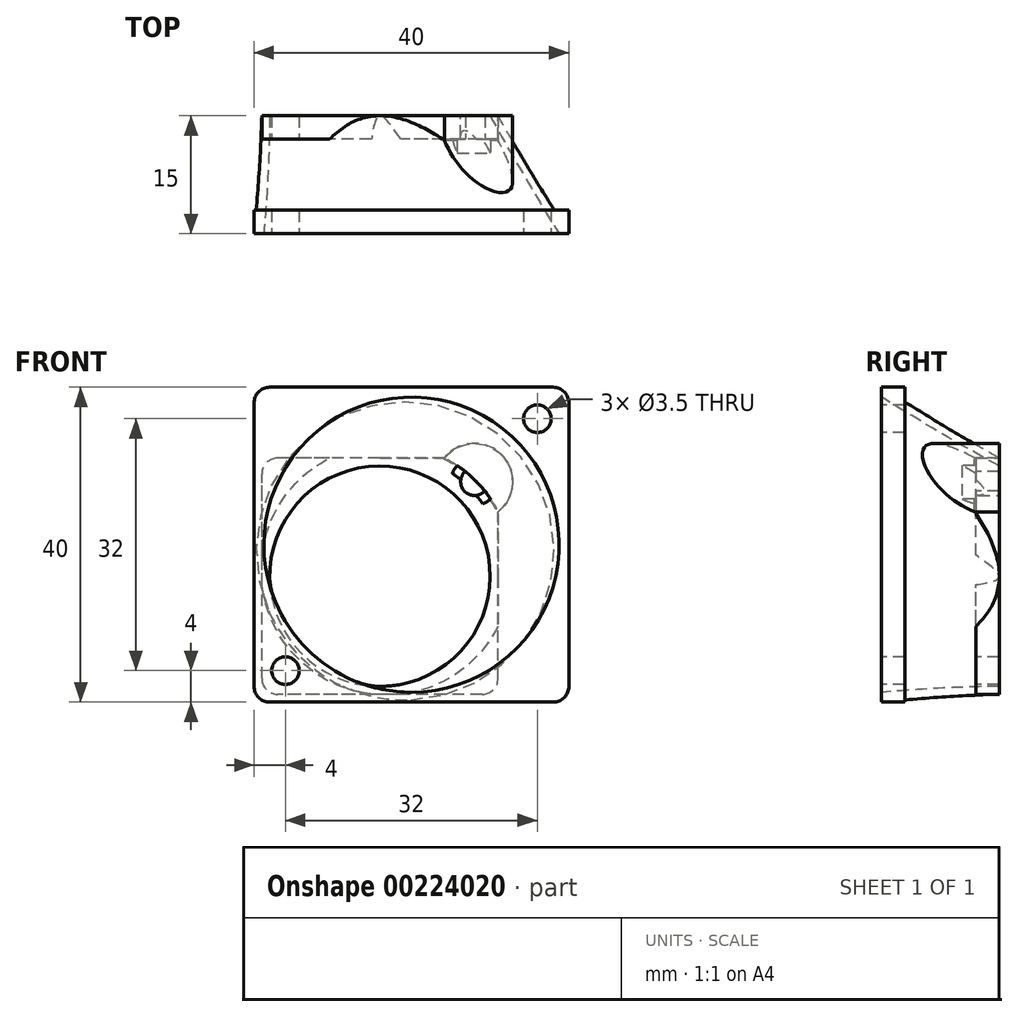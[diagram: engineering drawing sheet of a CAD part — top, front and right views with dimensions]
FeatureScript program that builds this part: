
annotation { "Feature Type Name" : "Feature", "Feature Type Description" : "" }
export const myFeature = defineFeature(function(context is Context, id is Id, definition is map)
    precondition{}
    {
        {
            var Q0;
            Q0=qCreatedBy(makeId("Front.planeOp"),FACE);
            var sketch = newSketch(context, id + "F0", { "sketchPlane" : qUnion([Q0])});
            skLineSegment(sketch, "E0.bottom", {"start": v(0, 0) * mm, "end": v(40, 0) * mm});
            skLineSegment(sketch, "E0.top", {"start": v(0, 40) * mm, "end": v(40, 40) * mm});
            skLineSegment(sketch, "E0.left", {"start": v(0, 0) * mm, "end": v(0, 40) * mm});
            skLineSegment(sketch, "E0.right", {"start": v(40, 0) * mm, "end": v(40, 40) * mm});
            skLineSegment(sketch, "E1", {"start": v(0, 0) * mm, "end": v(40, 40) * mm, "construction": true});
            skLineSegment(sketch, "E2", {"start": v(0, 40) * mm, "end": v(40, 0) * mm, "construction": true});
            skCircle(sketch, "E3", {"center": v(20, 20) * mm, "radius": 20 * mm});
            skSolve(sketch);
        }
        {
            var Q0;
            Q0=makeQuery(id+"F0.imprint","IMPRINT",FACE,{"disambiguationData":[TD([[makeQuery(id+"F0.imprint","IMPRINT",EDGE,{"derivedFrom":sQuery(id+"F0.wireOp",EDGE,"E0.bottom")}),1.0]])]});
            var Q1;
            {var subQ0=sQuery(id+"F0.wireOp",EDGE,"E0.right");var subQ1=sQuery(id+"F0.wireOp",EDGE,"E0.top");var subQ2=makeQuery(id+"F0.imprint","INTERSECT",VERTEX,{"derivedFrom":[subQ1,subQ0]});Q1=makeQuery(id+"F0.imprint","IMPRINT",FACE,{"disambiguationData":[TD([[makeQuery(id+"F0.imprint","IMPRINT",EDGE,{"disambiguationData":[TD([[subQ2,1.0]])],"derivedFrom":subQ1}),-1.0]])]});}
            var Q2;
            {var subQ0=sQuery(id+"F0.wireOp",EDGE,"E0.left");var subQ1=sQuery(id+"F0.wireOp",EDGE,"E0.top");var subQ2=makeQuery(id+"F0.imprint","INTERSECT",VERTEX,{"derivedFrom":[subQ1,subQ0]});Q2=makeQuery(id+"F0.imprint","IMPRINT",FACE,{"disambiguationData":[TD([[makeQuery(id+"F0.imprint","IMPRINT",EDGE,{"disambiguationData":[TD([[subQ2,-1.0]])],"derivedFrom":subQ1}),-1.0]])]});}
            var Q3;
            {var subQ0=sQuery(id+"F0.wireOp",EDGE,"E3");var subQ1=makeQuery(id+"F0.imprint","INTERSECT",VERTEX,{"derivedFrom":[sQuery(id+"F0.wireOp",EDGE,"E0.top"),subQ0]});Q3=makeQuery(id+"F0.imprint","IMPRINT",FACE,{"disambiguationData":[TD([[makeQuery(id+"F0.imprint","IMPRINT",EDGE,{"disambiguationData":[TD([[subQ1,1.0]])],"derivedFrom":subQ0}),1.0]])]});}
            extrude(context, id + "F1", {"entities" : qUnion([Q0, Q1, Q2, Q3]), "oppositeDirection" : true, "depth" : 3 * mm});
        }
        {
            var Q0;
            Q0=qCreatedBy(makeId("Front.planeOp"),FACE);
            cPlane(context, id + "F2", {"entities" : qUnion([Q0]), "cplaneType" : CPlaneType.OFFSET, "offset" : 15 * mm, "oppositeDirection" : true, "width" : 150 * mm, "height" : 150 * mm});
        }
        {
            var Q0;
            Q0=qCreatedBy(id+"F2.planeOp",FACE);
            var sketch = newSketch(context, id + "F3", { "sketchPlane" : qUnion([Q0])});
            skLineSegment(sketch, "E4.bottom", {"start": v(31, 31) * mm, "end": v(1, 31) * mm});
            skLineSegment(sketch, "E4.top", {"start": v(31, 1) * mm, "end": v(1, 1) * mm});
            skLineSegment(sketch, "E4.left", {"start": v(1, 1) * mm, "end": v(1, 31) * mm});
            skLineSegment(sketch, "E4.right", {"start": v(31, 1) * mm, "end": v(31, 31) * mm});
            skLineSegment(sketch, "E5", {"start": v(1, 1) * mm, "end": v(31, 31) * mm, "construction": true});
            skLineSegment(sketch, "E6", {"start": v(1, 31) * mm, "end": v(31, 1) * mm, "construction": true});
            skCircle(sketch, "E7", {"center": v(16, 16) * mm, "radius": 15 * mm});
            skSolve(sketch);
        }
        {
            var Q1;
            {var subQ0=sQuery(id+"F0.wireOp",EDGE,"E3");var subQ1=makeQuery(id+"F0.imprint","INTERSECT",VERTEX,{"derivedFrom":[sQuery(id+"F0.wireOp",EDGE,"E0.top"),subQ0]});Q1=makeQuery(id+"F0.imprint","IMPRINT",FACE,{"disambiguationData":[TD([[makeQuery(id+"F0.imprint","IMPRINT",EDGE,{"disambiguationData":[TD([[subQ1,1.0]])],"derivedFrom":subQ0}),1.0]])]});}
            var Q2;
            {var subQ0=sQuery(id+"F3.wireOp",EDGE,"E7");var subQ1=makeQuery(id+"F3.imprint","INTERSECT",VERTEX,{"derivedFrom":[sQuery(id+"F3.wireOp",EDGE,"E4.top"),subQ0]});Q2=makeQuery(id+"F3.imprint","IMPRINT",FACE,{"disambiguationData":[TD([[makeQuery(id+"F3.imprint","IMPRINT",EDGE,{"disambiguationData":[TD([[subQ1,1.0]])],"derivedFrom":subQ0}),1.0]])]});}
            loft(context, id + "F4", {"operationType" : NewBodyOperationType.ADD, "sheetProfilesArray" : [{ "sheetProfileEntities" : qUnion([Q1]) }, { "sheetProfileEntities" : qUnion([Q2]) }]});
        }
        {
            var Q0;
            Q0 = qSketchRegion(id + "F3", true);
            extrude(context, id + "F5", {"entities" : qUnion([Q0]), "operationType" : NewBodyOperationType.ADD, "depth" : 3 * mm});
        }
        {
            var Q0;
            {var subQ0=sQuery(id+"F0.wireOp",EDGE,"E3");var subQ1=makeQuery(id+"F0.imprint","INTERSECT",VERTEX,{"derivedFrom":[sQuery(id+"F0.wireOp",EDGE,"E0.top"),subQ0]});Q0=makeQuery(id+"F0.imprint","IMPRINT",FACE,{"disambiguationData":[TD([[makeQuery(id+"F0.imprint","IMPRINT",EDGE,{"disambiguationData":[TD([[subQ1,1.0]])],"derivedFrom":subQ0}),1.0]])]});}
            var sketch = newSketch(context, id + "F6", { "sketchPlane" : qUnion([Q0])});
            skPoint(sketch, "E8.0", {"position": v(20, 20) * mm});
            skCircle(sketch, "E9", {"center": v(20, 20) * mm, "radius": 18.75 * mm});
            skSolve(sketch);
        }
        {
            var Q0;
            {var subQ0=sQuery(id+"F3.wireOp",EDGE,"E7");var subQ1=makeQuery(id+"F3.imprint","INTERSECT",VERTEX,{"derivedFrom":[sQuery(id+"F3.wireOp",EDGE,"E4.top"),subQ0]});Q0=makeQuery(id+"F3.imprint","IMPRINT",FACE,{"disambiguationData":[TD([[makeQuery(id+"F3.imprint","IMPRINT",EDGE,{"disambiguationData":[TD([[subQ1,1.0]])],"derivedFrom":subQ0}),1.0]])]});}
            var sketch = newSketch(context, id + "F7", { "sketchPlane" : qUnion([Q0])});
            skPoint(sketch, "E10.0", {"position": v(16, 16) * mm});
            skCircle(sketch, "E11", {"center": v(16, 16) * mm, "radius": 14 * mm});
            skSolve(sketch);
        }
        {
            var Q1;
            Q1 = qSketchRegion(id + "F6", true);
            var Q2;
            Q2 = qSketchRegion(id + "F7", true);
            loft(context, id + "F8", {"operationType" : NewBodyOperationType.REMOVE, "sheetProfilesArray" : [{ "sheetProfileEntities" : qUnion([Q1]) }, { "sheetProfileEntities" : qUnion([Q2]) }]});
        }
        {
            var Q0;
            {var subQ0=sQuery(id+"F0.wireOp",EDGE,"E0.left");var subQ1=sQuery(id+"F0.wireOp",EDGE,"E0.bottom");var subQ2=makeQuery(id+"F0.imprint","INTERSECT",VERTEX,{"derivedFrom":[subQ1,subQ0]});Q0=makeQuery(id+"F0.imprint","IMPRINT",FACE,{"disambiguationData":[TD([[makeQuery(id+"F0.imprint","IMPRINT",EDGE,{"disambiguationData":[TD([[subQ2,-1.0]])],"derivedFrom":subQ1}),1.0]])]});}
            var sketch = newSketch(context, id + "F9", { "sketchPlane" : qUnion([Q0])});
            skCircle(sketch, "E12", {"center": v(4, 4) * mm, "radius": 1.75 * mm});
            skLineSegment(sketch, "E13.0", {"start": v(0, 0) * mm, "end": v(40, 40) * mm, "construction": true});
            skCircle(sketch, "E14", {"center": v(36, 36) * mm, "radius": 1.75 * mm});
            skSolve(sketch);
        }
        {
            var Q0;
            Q0 = qSketchRegion(id + "F9", true);
            extrude(context, id + "F10", {"entities" : qUnion([Q0]), "operationType" : NewBodyOperationType.REMOVE, "endBound" : BoundingType.THROUGH_ALL, "oppositeDirection" : true, "depth" : 25 * mm});
        }
        {
            var Q0;
            {var subQ0=sQuery(id+"F3.wireOp",EDGE,"E4.right");var subQ1=sQuery(id+"F3.wireOp",EDGE,"E4.bottom");var subQ2=makeQuery(id+"F3.imprint","INTERSECT",VERTEX,{"derivedFrom":[subQ1,subQ0]});Q0=makeQuery(id+"F3.imprint","IMPRINT",FACE,{"disambiguationData":[TD([[makeQuery(id+"F3.imprint","IMPRINT",EDGE,{"disambiguationData":[TD([[subQ2,-1.0]])],"derivedFrom":subQ1}),1.0]])]});}
            var sketch = newSketch(context, id + "F11", { "sketchPlane" : qUnion([Q0])});
            skLineSegment(sketch, "E15.0", {"start": v(1, 1) * mm, "end": v(31, 31) * mm, "construction": true});
            skCircle(sketch, "E16", {"center": v(28, 28) * mm, "radius": 1.75 * mm});
            skSolve(sketch);
        }
        {
            var Q0;
            Q0 = qSketchRegion(id + "F11", true);
            extrude(context, id + "F12", {"entities" : qUnion([Q0]), "operationType" : NewBodyOperationType.REMOVE, "endBound" : BoundingType.THROUGH_ALL, "depth" : 25 * mm});
        }
        {
            var Q0;
            {var subQ0=sQuery(id+"F0.wireOp",EDGE,"E0.right");var subQ1=sQuery(id+"F0.wireOp",EDGE,"E0.top");var subQ2=makeQuery(id+"F0.imprint","INTERSECT",VERTEX,{"derivedFrom":[subQ1,subQ0]});Q0=makeQuery(id+"F0.imprint","IMPRINT",FACE,{"disambiguationData":[TD([[makeQuery(id+"F0.imprint","IMPRINT",EDGE,{"disambiguationData":[TD([[subQ2,1.0]])],"derivedFrom":subQ1}),-1.0]])]});}
            var sketch = newSketch(context, id + "F13", { "sketchPlane" : qUnion([Q0])});
            skCircle(sketch, "E17.0", {"center": v(28, 28) * mm, "radius": 1.75 * mm, "construction": true});
            skCircle(sketch, "E18", {"center": v(28, 28) * mm, "radius": 3 * mm});
            skSolve(sketch);
        }
        {
            var Q0;
            Q0=makeQuery(id+"F13.imprint","IMPRINT",FACE,{"disambiguationData":[TD([[makeQuery(id+"F13.imprint","IMPRINT",EDGE,{"derivedFrom":sQuery(id+"F13.wireOp",EDGE,"E18")}),1.0]])]});
            var Q1;
            {var subQ0=sQuery(id+"F3.wireOp",EDGE,"E4.left");var subQ1=sQuery(id+"F3.wireOp",EDGE,"E4.top");var subQ2=sQuery(id+"F3.wireOp",EDGE,"E4.bottom");var subQ3=sQuery(id+"F3.wireOp",EDGE,"E4.right");Q1=makeQuery(id+"F5.boolean.opBoolean","SPLIT",FACE,{"disambiguationData":[TD([makeQuery(id+"F4.opLoft","SWEPT_FACE",FACE,{"disambiguationData":[OSD([sQuery(id+"F0.wireOp",EDGE,"E0.bottom"),sQuery(id+"F0.wireOp",EDGE,"E0.left"),sQuery(id+"F0.wireOp",EDGE,"E3"),subQ1,subQ0,sQuery(id+"F3.wireOp",EDGE,"E7")])]}),makeQuery(id+"F5.opExtrude","SWEPT_FACE",FACE,{"disambiguationData":[OSD([subQ2])]}),makeQuery(id+"F5.opExtrude","SWEPT_FACE",FACE,{"disambiguationData":[OSD([subQ3])]})])],"derivedFrom":makeQuery(id+"F5.opExtrude","CAP_FACE",FACE,{"disambiguationData":[OSD([subQ2,subQ1,subQ0,subQ3])],"isStart":false})});}
            extrude(context, id + "F14", {"entities" : qUnion([Q0]), "operationType" : NewBodyOperationType.REMOVE, "endBound" : BoundingType.UP_TO_SURFACE, "oppositeDirection" : true, "endBoundEntityFace" : qUnion([Q1]), "depth" : 12 * mm});
        }
        {
            var Q0;
            {var subQ0=sQuery(id+"F3.wireOp",EDGE,"E4.left");var subQ1=sQuery(id+"F3.wireOp",EDGE,"E4.top");var subQ2=sQuery(id+"F3.wireOp",EDGE,"E4.bottom");var subQ3=sQuery(id+"F3.wireOp",EDGE,"E4.right");Q0=makeQuery(id+"F14.boolean.opBoolean","MERGE",FACE,{"derivedFrom":[makeQuery(id+"F5.boolean.opBoolean","SPLIT",FACE,{"disambiguationData":[TD([makeQuery(id+"F4.opLoft","SWEPT_FACE",FACE,{"disambiguationData":[OSD([sQuery(id+"F0.wireOp",EDGE,"E0.bottom"),sQuery(id+"F0.wireOp",EDGE,"E0.left"),sQuery(id+"F0.wireOp",EDGE,"E3"),subQ1,subQ0,sQuery(id+"F3.wireOp",EDGE,"E7")])]}),makeQuery(id+"F5.opExtrude","SWEPT_FACE",FACE,{"disambiguationData":[OSD([subQ2])]}),makeQuery(id+"F5.opExtrude","SWEPT_FACE",FACE,{"disambiguationData":[OSD([subQ3])]})])],"derivedFrom":makeQuery(id+"F5.opExtrude","CAP_FACE",FACE,{"disambiguationData":[OSD([subQ2,subQ1,subQ0,subQ3])],"isStart":false})}),makeQuery(id+"F14.opExtrude","CAP_FACE",FACE,{"disambiguationData":[OSD([sQuery(id+"F13.wireOp",EDGE,"E18")])],"isStart":false})]});}
            var sketch = newSketch(context, id + "F15", { "sketchPlane" : qUnion([Q0])});
            skArc(sketch, "E19.0", {"start": v(30.03, 25.8) * mm, "mid": v(30.12, 30.12) * mm, "end": v(25.8, 30.03) * mm});
            skFitSpline(sketch, "E20.0", {"points": [v(24.17, 31) * mm, v(24.7, 30.73) * mm, v(25.2, 30.43) * mm, v(26.56, 29.52) * mm, v(27.37, 28.85) * mm, v(28.85, 27.37) * mm, v(29.52, 26.56) * mm, v(30.43, 25.2) * mm, v(30.73, 24.7) * mm, v(31, 24.17) * mm]});
            skFitSpline(sketch, "E21.0", {"points": [v(24.17, 31) * mm, v(24.7, 30.73) * mm, v(25.2, 30.43) * mm, v(26.56, 29.52) * mm, v(27.37, 28.85) * mm, v(28.85, 27.37) * mm, v(29.52, 26.56) * mm, v(30.43, 25.2) * mm, v(30.73, 24.7) * mm, v(31, 24.17) * mm]});
            skArc(sketch, "E22", {"start": v(24.17, 31) * mm, "mid": v(31.44, 31.44) * mm, "end": v(31, 24.17) * mm});
            skSolve(sketch);
        }
        {
            var Q0;
            Q0 = qSketchRegion(id + "F15", true);
            var Q1;
            {var subQ0=sQuery(id+"F3.wireOp",EDGE,"E4.right");var subQ1=sQuery(id+"F3.wireOp",EDGE,"E4.left");var subQ2=sQuery(id+"F3.wireOp",EDGE,"E4.top");var subQ3=sQuery(id+"F3.wireOp",EDGE,"E4.bottom");var subQ4=sQuery(id+"F3.wireOp",EDGE,"E7");var subQ5=makeQuery(id+"F3.imprint","INTERSECT",VERTEX,{"derivedFrom":[subQ3,subQ4]});Q1=makeQuery(id+"F5.boolean.opBoolean","MERGE",FACE,{"derivedFrom":[makeQuery(id+"F4.opLoft","CAP_FACE",FACE,{"disambiguationData":[OSD([makeQuery(id+"F3.imprint","IMPRINT",FACE,{"disambiguationData":[TD([[makeQuery(id+"F3.imprint","IMPRINT",EDGE,{"disambiguationData":[TD([[subQ5,1.0]])],"derivedFrom":subQ4}),1.0]])]})])],"isStart":true}),makeQuery(id+"F5.opExtrude","CAP_FACE",FACE,{"disambiguationData":[OSD([subQ3,subQ2,subQ1,subQ0])],"isStart":true})]});}
            var Q2;
            Q2=makeQuery(id+"F8.boolean.opBoolean","COPY",FACE,{"derivedFrom":makeQuery(id+"F8.opLoft","SWEPT_FACE",FACE,{"disambiguationData":[OSD([sQuery(id+"F6.wireOp",EDGE,"E9"),sQuery(id+"F7.wireOp",EDGE,"E11")])]})});
            extrude(context, id + "F16", {"entities" : qUnion([Q0]), "operationType" : NewBodyOperationType.ADD, "endBound" : BoundingType.UP_TO_SURFACE, "oppositeDirection" : true, "endBoundEntityFace" : qUnion([Q1]), "depth" : 25 * mm, "hasSecondDirection" : true, "secondDirectionBound" : SecondDirectionBoundingType.UP_TO_SURFACE, "secondDirectionOppositeDirection" : false, "secondDirectionBoundEntityFace" : qUnion([Q2]), "secondDirectionDepth" : 10.4 * mm});
        }
        {
            var Q0;
            Q0=makeQuery(id+"F5.opExtrude","SWEPT_EDGE",EDGE,{"disambiguationData":[OSD([sQuery(id+"F3.wireOp",EDGE,"E4.bottom"),sQuery(id+"F3.wireOp",EDGE,"E4.left")])]});
            var Q1;
            Q1=makeQuery(id+"F5.opExtrude","SWEPT_EDGE",EDGE,{"disambiguationData":[OSD([sQuery(id+"F3.wireOp",EDGE,"E4.top"),sQuery(id+"F3.wireOp",EDGE,"E4.left")])]});
            var Q2;
            Q2=makeQuery(id+"F1.opExtrude","SWEPT_EDGE",EDGE,{"disambiguationData":[OSD([sQuery(id+"F0.wireOp",EDGE,"E0.top"),sQuery(id+"F0.wireOp",EDGE,"E0.left")])]});
            var Q3;
            Q3=makeQuery(id+"F1.opExtrude","SWEPT_EDGE",EDGE,{"disambiguationData":[OSD([sQuery(id+"F0.wireOp",EDGE,"E0.bottom"),sQuery(id+"F0.wireOp",EDGE,"E0.left")])]});
            var Q4;
            Q4=makeQuery(id+"F1.opExtrude","SWEPT_EDGE",EDGE,{"disambiguationData":[OSD([sQuery(id+"F0.wireOp",EDGE,"E0.top"),sQuery(id+"F0.wireOp",EDGE,"E0.right")])]});
            var Q5;
            Q5=makeQuery(id+"F1.opExtrude","SWEPT_EDGE",EDGE,{"disambiguationData":[OSD([sQuery(id+"F0.wireOp",EDGE,"E0.bottom"),sQuery(id+"F0.wireOp",EDGE,"E0.right")])]});
            var Q6;
            Q6=makeQuery(id+"F5.opExtrude","SWEPT_EDGE",EDGE,{"disambiguationData":[OSD([sQuery(id+"F3.wireOp",EDGE,"E4.top"),sQuery(id+"F3.wireOp",EDGE,"E4.right")])]});
            fillet(context, id + "F17", {"entities" : qUnion([Q0, Q1, Q2, Q3, Q4, Q5, Q6]), "radius" : 2 * mm, "tangentPropagation" : true, "allowEdgeOverflow" : false});
        }
    });
